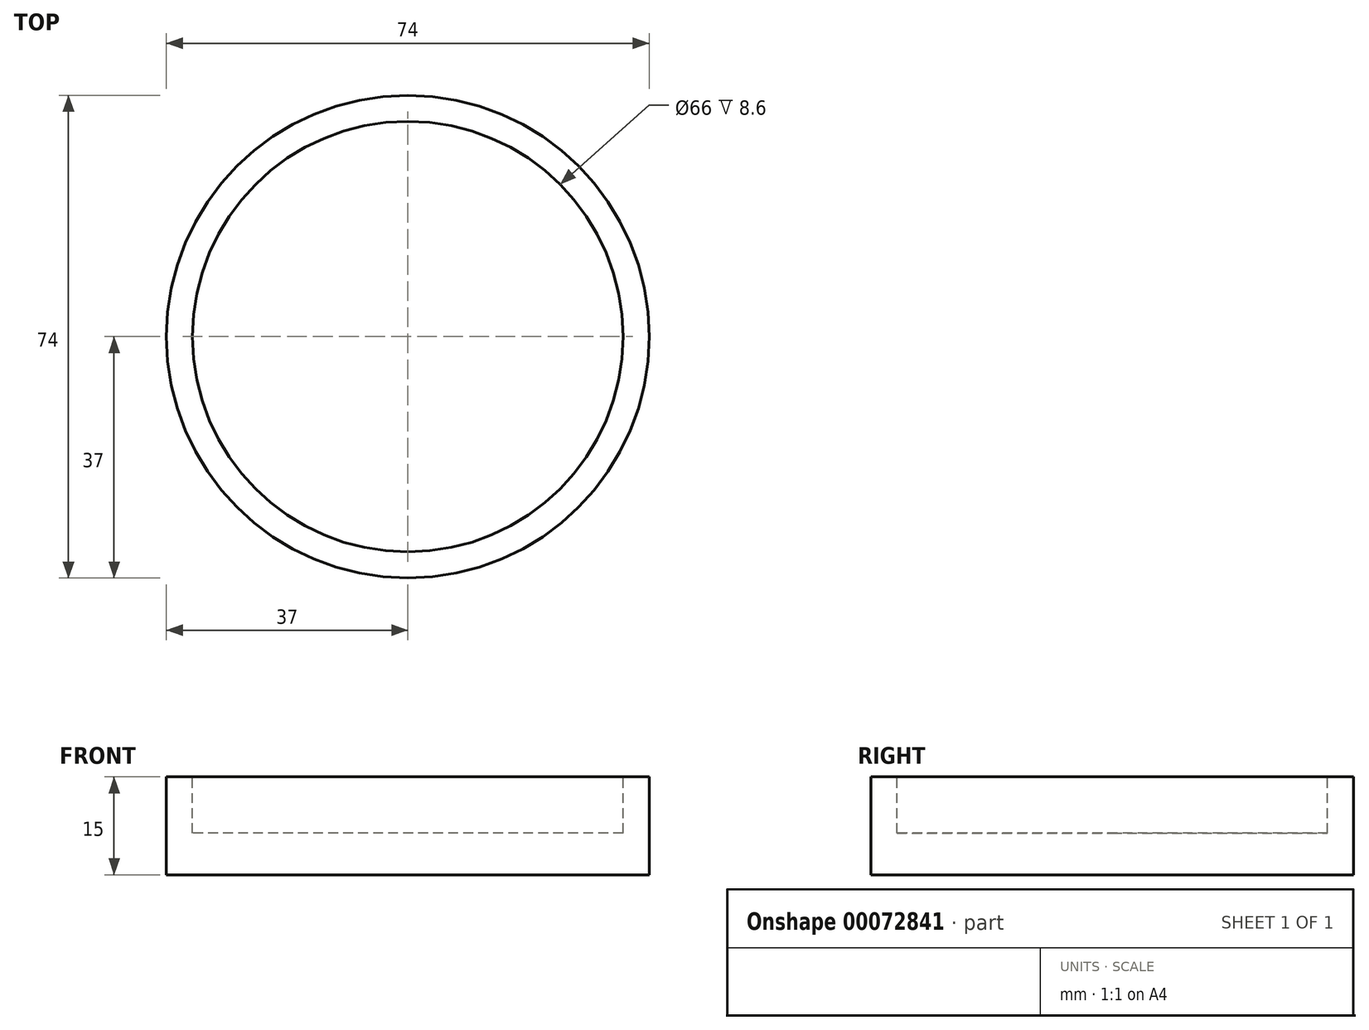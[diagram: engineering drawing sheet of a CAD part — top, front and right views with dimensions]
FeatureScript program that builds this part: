
annotation { "Feature Type Name" : "Feature", "Feature Type Description" : "" }
export const myFeature = defineFeature(function(context is Context, id is Id, definition is map)
    precondition{}
    {
        {
            var Q0;
            Q0=qCreatedBy(makeId("Front.planeOp"),FACE);
            var sketch = newSketch(context, id + "F0", { "sketchPlane" : qUnion([Q0])});
            skLineSegment(sketch, "E0", {"start": v(0, 0) * mm, "end": v(-37, 0) * mm});
            skLineSegment(sketch, "E1", {"start": v(-37, 0) * mm, "end": v(-37, 15) * mm});
            skLineSegment(sketch, "E2", {"start": v(-37, 15) * mm, "end": v(-33, 15) * mm});
            skLineSegment(sketch, "E3", {"start": v(-33, 15) * mm, "end": v(-33, 6.4) * mm});
            skLineSegment(sketch, "E4", {"start": v(-33, 6.4) * mm, "end": v(0, 6.4) * mm});
            skLineSegment(sketch, "E5", {"start": v(0, 6.4) * mm, "end": v(0, 0) * mm});
            skSolve(sketch);
        }
        {
            var Q0;
            Q0=makeQuery(id+"F0.imprint","IMPRINT",FACE,{"disambiguationData":[TD([[makeQuery(id+"F0.imprint","IMPRINT",EDGE,{"derivedFrom":sQuery(id+"F0.wireOp",EDGE,"E0")}),-1.0]])]});
            var Q1;
            Q1=sQuery(id+"F0.wireOp",EDGE,"E5");
            revolve(context, id + "F1", {"entities" : qUnion([Q0]), "axis" : qUnion([Q1]), "revolveType" : RevolveType.FULL});
        }
    });
